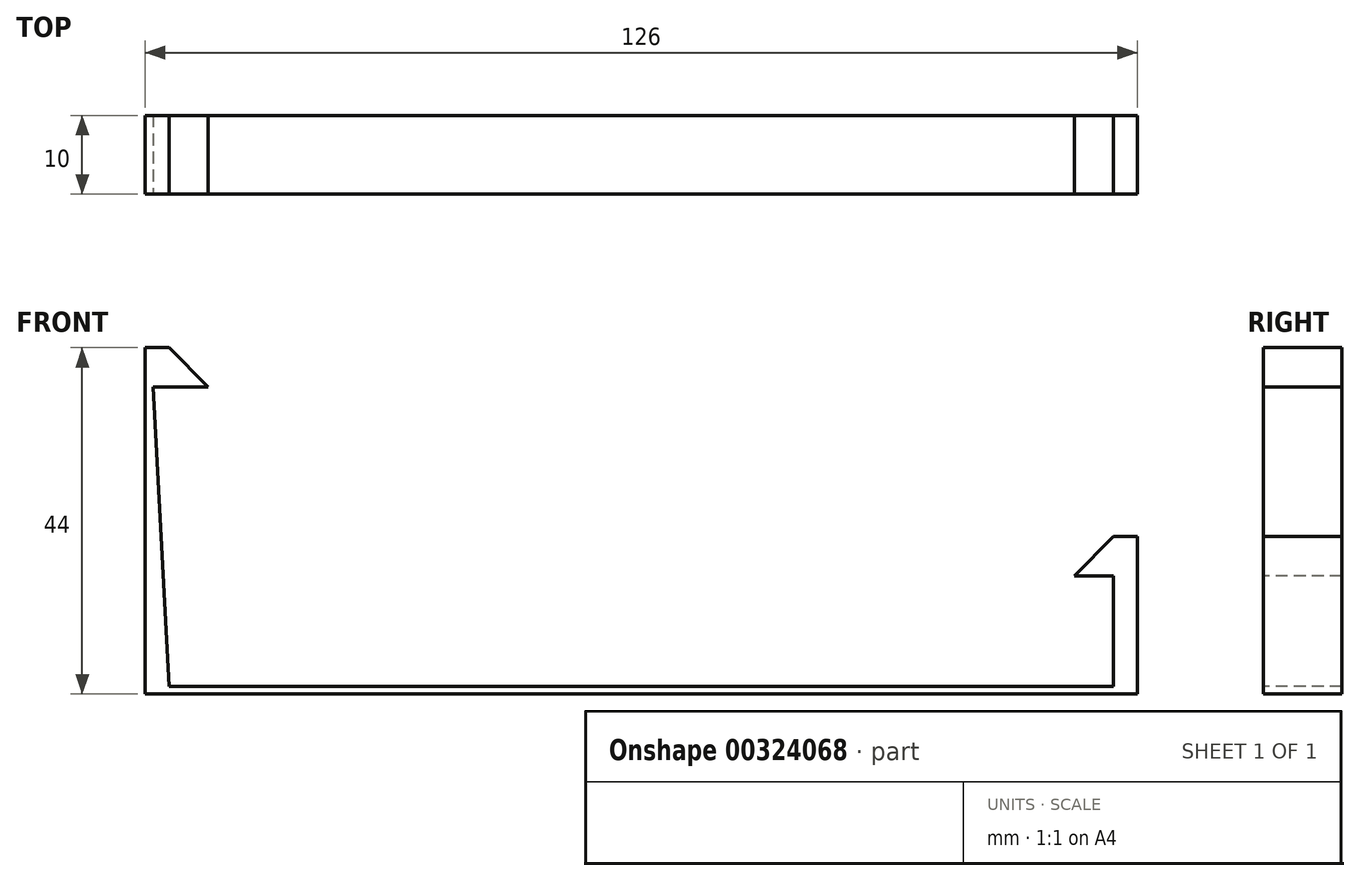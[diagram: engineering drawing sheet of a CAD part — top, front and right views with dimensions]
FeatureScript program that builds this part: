
annotation { "Feature Type Name" : "Feature", "Feature Type Description" : "" }
export const myFeature = defineFeature(function(context is Context, id is Id, definition is map)
    precondition{}
    {
        {
            var Q0;
            Q0=qCreatedBy(makeId("Front.planeOp"),FACE);
            var sketch = newSketch(context, id + "F0", { "sketchPlane" : qUnion([Q0])});
            skLineSegment(sketch, "E0.bottom", {"start": v(-63, 1) * mm, "end": v(63, 1) * mm});
            skLineSegment(sketch, "E0.top", {"start": v(-63, 0) * mm, "end": v(63, 0) * mm});
            skLineSegment(sketch, "E0.left", {"start": v(-63, 1) * mm, "end": v(-63, 0) * mm});
            skLineSegment(sketch, "E0.right", {"start": v(63, 1) * mm, "end": v(63, 0) * mm});
            skPoint(sketch, "E1", {"position": v(0, 0) * mm});
            skSolve(sketch);
        }
        {
            var Q0;
            Q0=qSketchRegion(id+"F0",true);
            extrude(context, id + "F1", {"entities" : qUnion([Q0]), "depth" : 10 * mm});
        }
        {
            var Q0;
            Q0=makeQuery(id+"F1.opExtrude","SWEPT_FACE",FACE,{"disambiguationData":[OSD([sQuery(id+"F0.wireOp",EDGE,"E0.bottom")])]});
            var sketch = newSketch(context, id + "F2", { "sketchPlane" : qUnion([Q0])});
            skLineSegment(sketch, "E2.bottom", {"start": v(-63, 0) * mm, "end": v(-60, 0) * mm});
            skLineSegment(sketch, "E2.top", {"start": v(-63, -10) * mm, "end": v(-60, -10) * mm});
            skLineSegment(sketch, "E2.left", {"start": v(-63, 0) * mm, "end": v(-63, -10) * mm});
            skLineSegment(sketch, "E2.right", {"start": v(-60, 0) * mm, "end": v(-60, -10) * mm});
            skLineSegment(sketch, "E3.bottom", {"start": v(63, 0) * mm, "end": v(60, 0) * mm});
            skLineSegment(sketch, "E3.top", {"start": v(63, -10) * mm, "end": v(60, -10) * mm});
            skLineSegment(sketch, "E3.left", {"start": v(63, 0) * mm, "end": v(63, -10) * mm});
            skLineSegment(sketch, "E3.right", {"start": v(60, 0) * mm, "end": v(60, -10) * mm});
            skSolve(sketch);
        }
        {
            var Q0;
            Q0=makeQuery(id+"F2.imprint","IMPRINT",FACE,{"disambiguationData":[TD([[makeQuery(id+"F2.imprint","IMPRINT",EDGE,{"derivedFrom":sQuery(id+"F2.wireOp",EDGE,"E2.bottom")}),-1.0]])]});
            extrude(context, id + "F3", {"entities" : qUnion([Q0]), "operationType" : NewBodyOperationType.ADD, "depth" : 43 * mm});
        }
        {
            var Q0;
            Q0=makeQuery(id+"F2.imprint","IMPRINT",FACE,{"disambiguationData":[TD([[makeQuery(id+"F2.imprint","IMPRINT",EDGE,{"derivedFrom":sQuery(id+"F2.wireOp",EDGE,"E3.bottom")}),-1.0]])]});
            extrude(context, id + "F4", {"entities" : qUnion([Q0]), "operationType" : NewBodyOperationType.ADD, "depth" : 19 * mm});
        }
        {
            var Q0;
            Q0=makeQuery(id+"F4.boolean.opBoolean","MERGE",FACE,{"derivedFrom":[makeQuery(id+"F3.boolean.opBoolean","MERGE",FACE,{"derivedFrom":[makeQuery(id+"F1.opExtrude","CAP_FACE",FACE,{"disambiguationData":[OSD([sQuery(id+"F0.wireOp",EDGE,"E0.bottom"),sQuery(id+"F0.wireOp",EDGE,"E0.top"),sQuery(id+"F0.wireOp",EDGE,"E0.left"),sQuery(id+"F0.wireOp",EDGE,"E0.right")])],"isStart":false}),makeQuery(id+"F3.opExtrude","SWEPT_FACE",FACE,{"disambiguationData":[OSD([sQuery(id+"F2.wireOp",EDGE,"E2.top")])]})]}),makeQuery(id+"F4.opExtrude","SWEPT_FACE",FACE,{"disambiguationData":[OSD([sQuery(id+"F2.wireOp",EDGE,"E3.top")])]})]});
            var sketch = newSketch(context, id + "F5", { "sketchPlane" : qUnion([Q0])});
            skLineSegment(sketch, "E4", {"start": v(-60, 44) * mm, "end": v(-55, 39) * mm});
            skLineSegment(sketch, "E5", {"start": v(-55, 39) * mm, "end": v(-60, 39) * mm});
            skLineSegment(sketch, "E6", {"start": v(60, 20) * mm, "end": v(55, 15) * mm});
            skLineSegment(sketch, "E7", {"start": v(55, 15) * mm, "end": v(60, 15) * mm});
            skSolve(sketch);
        }
        {
            var Q0;
            {var subQ0=sQuery(id+"F5.wireOp",EDGE,"E4");Q0=makeQuery(id+"F5.imprint","IMPRINT",FACE,{"disambiguationData":[TD([[makeQuery(id+"F5.imprint","IMPRINT",EDGE,{"derivedFrom":subQ0}),-1.0]])]});}
            extrude(context, id + "F6", {"entities" : qUnion([Q0]), "operationType" : NewBodyOperationType.ADD, "oppositeDirection" : true, "depth" : 10 * mm});
        }
        {
            var Q0;
            {var subQ0=sQuery(id+"F5.wireOp",EDGE,"E6");Q0=makeQuery(id+"F5.imprint","IMPRINT",FACE,{"disambiguationData":[TD([[makeQuery(id+"F5.imprint","IMPRINT",EDGE,{"derivedFrom":subQ0}),1.0]])]});}
            extrude(context, id + "F7", {"entities" : qUnion([Q0]), "operationType" : NewBodyOperationType.ADD, "oppositeDirection" : true, "depth" : 10 * mm});
        }
        {
            var Q0;
            {var subQ0=sQuery(id+"F2.wireOp",EDGE,"E3.top");var subQ1=sQuery(id+"F0.wireOp",EDGE,"E0.bottom");var subQ2=sQuery(id+"F2.wireOp",EDGE,"E2.top");Q0=makeQuery(id+"F7.boolean.opBoolean","MERGE",FACE,{"derivedFrom":[makeQuery(id+"F6.boolean.opBoolean","MERGE",FACE,{"derivedFrom":[makeQuery(id+"F4.boolean.opBoolean","MERGE",FACE,{"derivedFrom":[makeQuery(id+"F3.boolean.opBoolean","MERGE",FACE,{"derivedFrom":[makeQuery(id+"F1.opExtrude","CAP_FACE",FACE,{"disambiguationData":[OSD([subQ1,sQuery(id+"F0.wireOp",EDGE,"E0.top"),sQuery(id+"F0.wireOp",EDGE,"E0.left"),sQuery(id+"F0.wireOp",EDGE,"E0.right")])],"isStart":false}),makeQuery(id+"F3.opExtrude","SWEPT_FACE",FACE,{"disambiguationData":[OSD([subQ2])]})]}),makeQuery(id+"F4.opExtrude","SWEPT_FACE",FACE,{"disambiguationData":[OSD([subQ0])]})]}),makeQuery(id+"F6.opExtrude","CAP_FACE",FACE,{"disambiguationData":[OSD([subQ1,subQ2,sQuery(id+"F2.wireOp",EDGE,"E2.right"),sQuery(id+"F5.wireOp",EDGE,"E4"),sQuery(id+"F5.wireOp",EDGE,"E5")])],"isStart":true})]}),makeQuery(id+"F7.opExtrude","CAP_FACE",FACE,{"disambiguationData":[OSD([subQ1,subQ0,sQuery(id+"F2.wireOp",EDGE,"E3.right"),sQuery(id+"F5.wireOp",EDGE,"E6"),sQuery(id+"F5.wireOp",EDGE,"E7")])],"isStart":true})]});}
            var sketch = newSketch(context, id + "F8", { "sketchPlane" : qUnion([Q0])});
            skLineSegment(sketch, "E8", {"start": v(-60, 1) * mm, "end": v(-62, 39) * mm});
            skLineSegment(sketch, "E9", {"start": v(-62, 39) * mm, "end": v(-60, 39) * mm});
            skLineSegment(sketch, "E10", {"start": v(-60, 39) * mm, "end": v(-60, 1) * mm});
            skSolve(sketch);
        }
        {
            var Q0;
            Q0=qSketchRegion(id+"F8",true);
            extrude(context, id + "F9", {"entities" : qUnion([Q0]), "operationType" : NewBodyOperationType.REMOVE, "oppositeDirection" : true, "depth" : 25 * mm});
        }
    });
